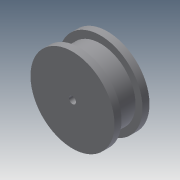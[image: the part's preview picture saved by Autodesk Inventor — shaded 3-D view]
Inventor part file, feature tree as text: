
AUTODESK INVENTOR PART (.ipt)
format: ipt  version: 2015 (Build 190159000, 159)  size: 101,888 bytes
history: native  units: mm
features: extrude x4, sketch x4
ambient origin geometry x8: Origin, YZ Plane, XZ Plane, XY Plane, X Axis, Y Axis, Z Axis, Center Point
bodies: Solid1 (feature_tree)
feature tree (8):
  extrude  "Extrusion1"  Depth=10.0mm TaperAngle=0.0deg
  extrude  "Extrusion2"  Depth=30.0mm TaperAngle=0.0deg
  extrude  "Extrusion3"  Depth=10.0mm TaperAngle=0.0deg
  extrude  "Extrusion4"  Depth=10.0mm
  sketch  "Sketch1"  dims[d0=120.0mm d1=10.0mm d2=0.0mm]
  sketch  "Sketch2"  dims[d3=100.0mm d4=30.0mm d5=0.0mm]
  sketch  "Sketch3"  dims[d6=120.0mm d7=10.0mm d8=0.0mm]
  sketch  "Sketch5"  dims[d9=10.0mm d10=10.0mm d11=10.0mm d12=0.0mm]
